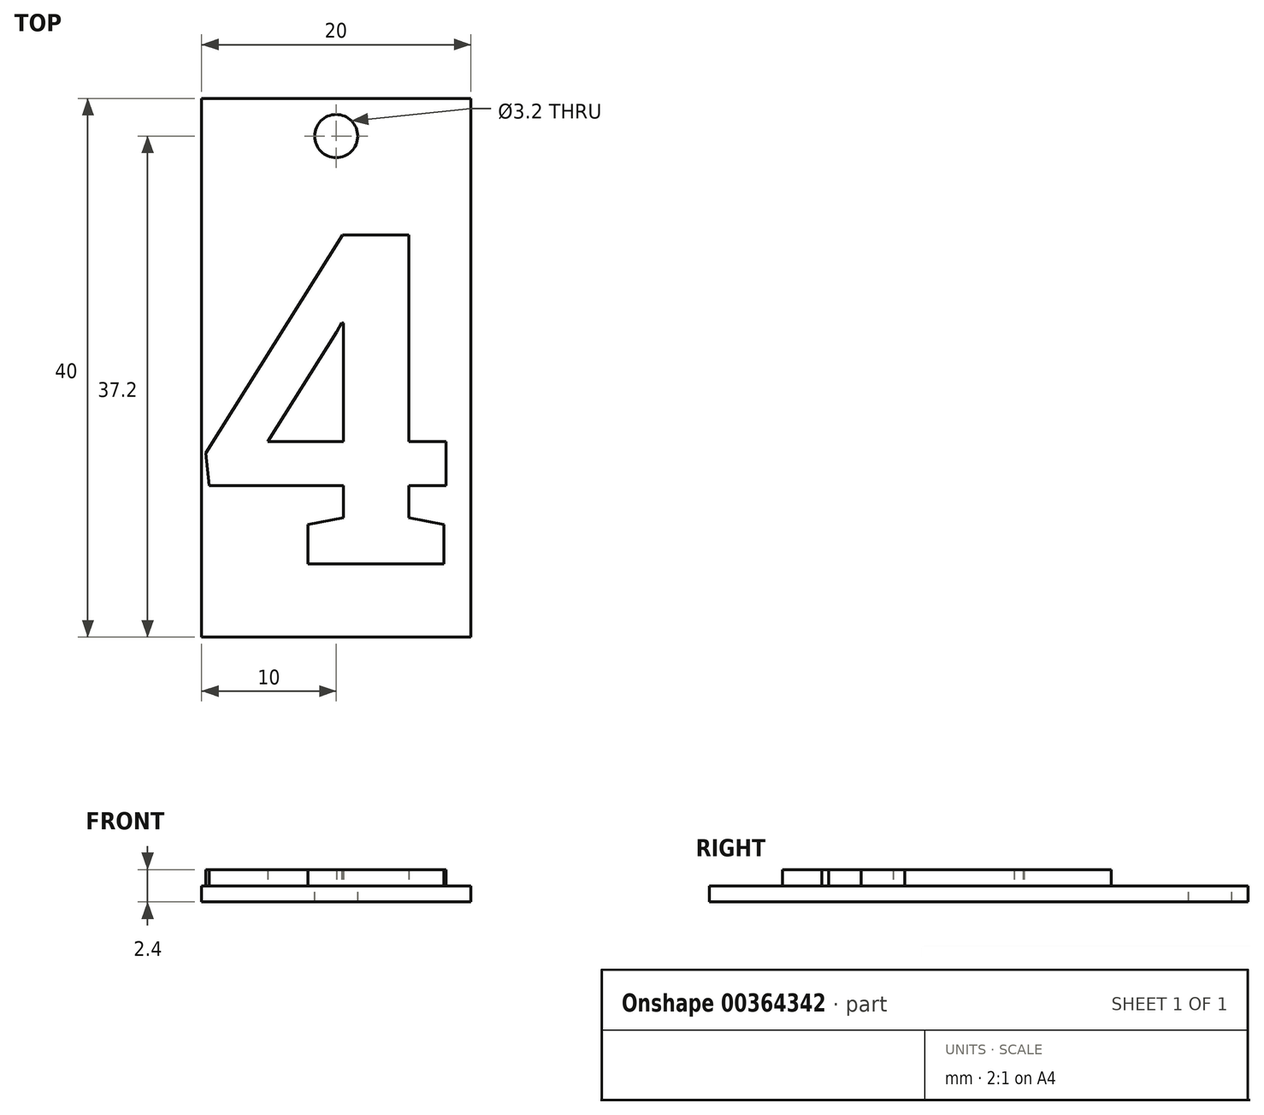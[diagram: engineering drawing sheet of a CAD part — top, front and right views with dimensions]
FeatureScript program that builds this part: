
annotation { "Feature Type Name" : "Feature", "Feature Type Description" : "" }
export const myFeature = defineFeature(function(context is Context, id is Id, definition is map)
    precondition{}
    {
        {
            var Q0;
            Q0=qCreatedBy(makeId("Top.planeOp"),FACE);
            var sketch = newSketch(context, id + "F0", { "sketchPlane" : qUnion([Q0])});
            skLineSegment(sketch, "E0.bottom", {"start": v(10, -20) * mm, "end": v(-10, -20) * mm});
            skLineSegment(sketch, "E0.top", {"start": v(10, 20) * mm, "end": v(-10, 20) * mm});
            skLineSegment(sketch, "E0.left", {"start": v(10, -20) * mm, "end": v(10, 20) * mm});
            skLineSegment(sketch, "E0.right", {"start": v(-10, -20) * mm, "end": v(-10, 20) * mm});
            skPoint(sketch, "E0.middle", {"position": v(0, 0) * mm});
            skCircle(sketch, "E1", {"center": v(0, 17.2) * mm, "radius": 1.6 * mm});
            skLineSegment(sketch, "E2", {"start": v(0, -20) * mm, "end": v(0, 15.6) * mm, "construction": true});
            skLineSegment(sketch, "E3", {"start": v(-10, -2.2) * mm, "end": v(10, -2.2) * mm, "construction": true});
            skPoint(sketch, "E3.startSnap0", {"position": v(0, -2.2) * mm});
            skLineSegment(sketch, "E4", {"start": v(10, -2.2) * mm, "end": v(-10, -2.2) * mm, "construction": true});
            skText(sketch, "E5", { "text": "4", "fontName": "RobotoSlab-Bold.ttf"});
            skLineSegment(sketch, "E6", {"start": v(-10.28, 10.17) * mm, "end": v(10.28, -14.57) * mm, "construction": true});
            skLineSegment(sketch, "E7", {"start": v(10.28, 10.17) * mm, "end": v(-10.28, -14.57) * mm, "construction": true});
            const initialGuessF0  = {"E5": [-0.01028, -0.01457, 1, 0, 0.02473]};
            skSetInitialGuess(sketch, initialGuessF0);
            skSolve(sketch);
        }
        {
            var Q0;
            Q0=makeQuery(id+"F0.imprint","IMPRINT",FACE,{"disambiguationData":[TD([[makeQuery(id+"F0.imprint","IMPRINT",EDGE,{"derivedFrom":sQuery(id+"F0.wireOp",EDGE,"E0.bottom")}),-1.0]])]});
            var Q1;
            Q1=makeQuery(id+"F0.imprint","IMPRINT",FACE,{"disambiguationData":[TD([[makeQuery(id+"F0.imprint","IMPRINT",EDGE,{"derivedFrom":sQuery(id+"F0.wireOp",EDGE,"E5.sketch_text.stroke-0")}),-1.0]])]});
            var Q2;
            Q2=makeQuery(id+"F0.imprint","IMPRINT",FACE,{"disambiguationData":[TD([[makeQuery(id+"F0.imprint","IMPRINT",EDGE,{"derivedFrom":sQuery(id+"F0.wireOp",EDGE,"E5.sketch_text.stroke-15")}),1.0]])]});
            extrude(context, id + "F1", {"entities" : qUnion([Q0, Q1, Q2]), "oppositeDirection" : true, "depth" : 1.2 * mm});
        }
        {
            var Q0;
            Q0=makeQuery(id+"F0.imprint","IMPRINT",FACE,{"disambiguationData":[TD([[makeQuery(id+"F0.imprint","IMPRINT",EDGE,{"derivedFrom":sQuery(id+"F0.wireOp",EDGE,"E5.sketch_text.stroke-0")}),-1.0]])]});
            extrude(context, id + "F2", {"entities" : qUnion([Q0]), "operationType" : NewBodyOperationType.ADD, "depth" : 1.2 * mm});
        }
    });
